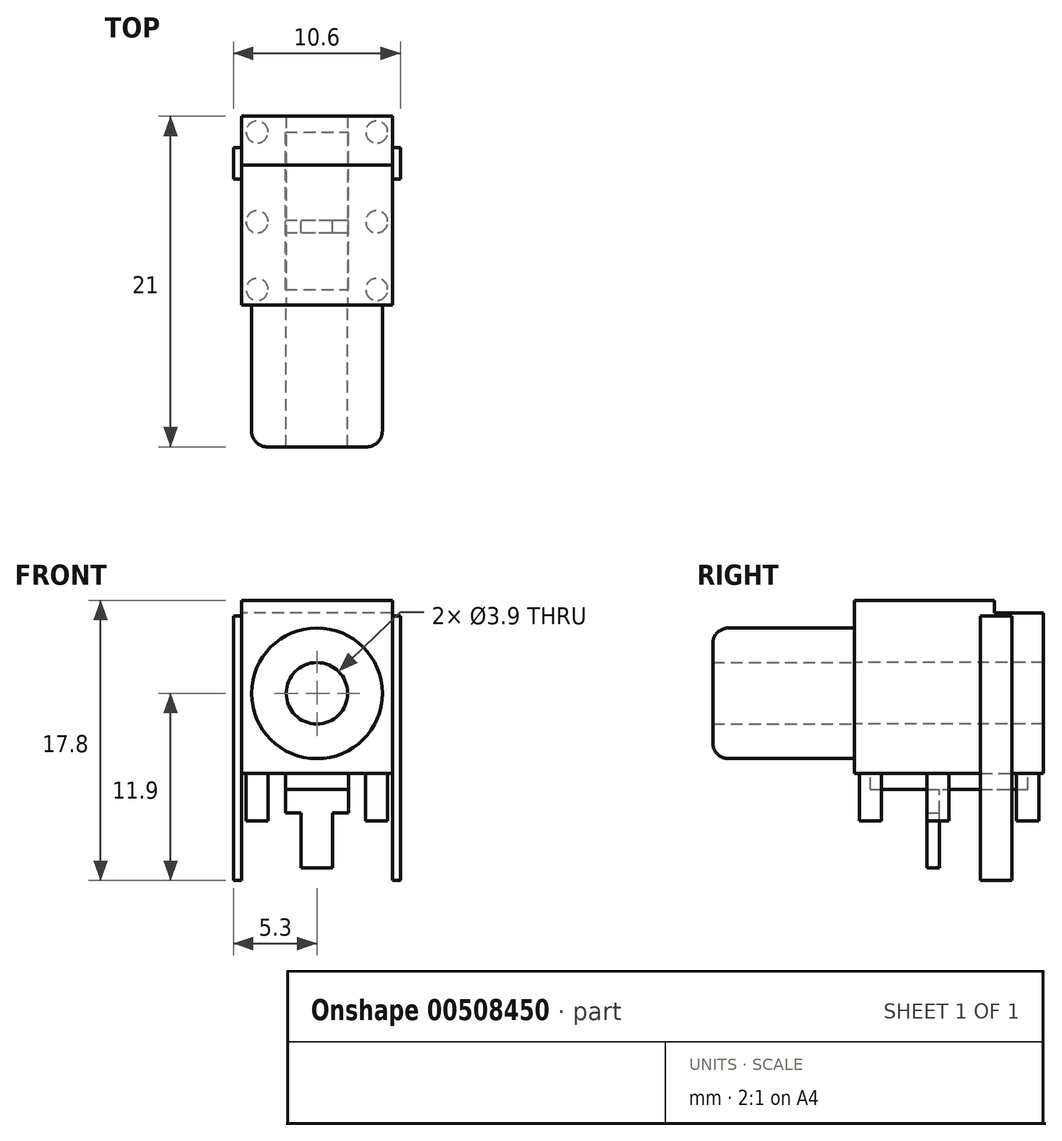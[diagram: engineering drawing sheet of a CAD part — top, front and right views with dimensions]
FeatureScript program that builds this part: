
annotation { "Feature Type Name" : "Feature", "Feature Type Description" : "" }
export const myFeature = defineFeature(function(context is Context, id is Id, definition is map)
    precondition{}
    {
        {
            var Q0;
            Q0=qCreatedBy(makeId("Front.planeOp"),FACE);
            var sketch = newSketch(context, id + "F0", { "sketchPlane" : qUnion([Q0])});
            skLineSegment(sketch, "E0.bottom", {"start": v(-4.8, 5.9) * mm, "end": v(4.8, 5.9) * mm});
            skLineSegment(sketch, "E0.top", {"start": v(-4.8, -5.1) * mm, "end": v(4.8, -5.1) * mm});
            skLineSegment(sketch, "E0.left", {"start": v(-4.8, 5.9) * mm, "end": v(-4.8, -5.1) * mm});
            skLineSegment(sketch, "E0.right", {"start": v(4.8, 5.9) * mm, "end": v(4.8, -5.1) * mm});
            skPoint(sketch, "E1", {"position": v(0, -5.1) * mm});
            skLineSegment(sketch, "E2", {"start": v(0, -5.1) * mm, "end": v(0, 0) * mm, "construction": true});
            skSolve(sketch);
        }
        {
            var Q0;
            Q0=makeQuery(id+"F0.imprint","IMPRINT",FACE,{"disambiguationData":[TD([[makeQuery(id+"F0.imprint","IMPRINT",EDGE,{"derivedFrom":sQuery(id+"F0.wireOp",EDGE,"E0.bottom")}),-1.0]])]});
            extrude(context, id + "F1", {"entities" : qUnion([Q0]), "depth" : 8.9 * mm});
        }
        {
            var Q0;
            Q0=makeQuery(id+"F1.opExtrude","CAP_FACE",FACE,{"disambiguationData":[OSD([sQuery(id+"F0.wireOp",EDGE,"E0.bottom"),sQuery(id+"F0.wireOp",EDGE,"E0.top"),sQuery(id+"F0.wireOp",EDGE,"E0.left"),sQuery(id+"F0.wireOp",EDGE,"E0.right")])],"isStart":true});
            var sketch = newSketch(context, id + "F2", { "sketchPlane" : qUnion([Q0])});
            skLineSegment(sketch, "E3.bottom", {"start": v(-4.8, -5.1) * mm, "end": v(4.8, -5.1) * mm});
            skLineSegment(sketch, "E3.top", {"start": v(-4.8, 5.1) * mm, "end": v(4.8, 5.1) * mm});
            skLineSegment(sketch, "E3.left", {"start": v(-4.8, -5.1) * mm, "end": v(-4.8, 5.1) * mm});
            skLineSegment(sketch, "E3.right", {"start": v(4.8, -5.1) * mm, "end": v(4.8, 5.1) * mm});
            skSolve(sketch);
        }
        {
            var Q0;
            Q0=makeQuery(id+"F2.imprint","IMPRINT",FACE,{"disambiguationData":[TD([[makeQuery(id+"F2.imprint","IMPRINT",EDGE,{"derivedFrom":sQuery(id+"F2.wireOp",EDGE,"E3.bottom")}),-1.0]])]});
            extrude(context, id + "F3", {"entities" : qUnion([Q0]), "operationType" : NewBodyOperationType.ADD, "depth" : 3.1 * mm});
        }
        {
            var Q0;
            Q0=makeQuery(id+"F3.boolean.opBoolean","MERGE",FACE,{"derivedFrom":[makeQuery(id+"F1.opExtrude","SWEPT_FACE",FACE,{"disambiguationData":[OSD([sQuery(id+"F0.wireOp",EDGE,"E0.top")])]}),makeQuery(id+"F3.opExtrude","SWEPT_FACE",FACE,{"disambiguationData":[OSD([sQuery(id+"F2.wireOp",EDGE,"E3.bottom")])]})]});
            var sketch = newSketch(context, id + "F4", { "sketchPlane" : qUnion([Q0])});
            skLineSegment(sketch, "E4", {"start": v(-3.8, 8.9) * mm, "end": v(-3.8, -3.1) * mm, "construction": true});
            skLineSegment(sketch, "E5", {"start": v(-3.8, 8.9) * mm, "end": v(-4.8, 8.9) * mm, "construction": true});
            skLineSegment(sketch, "E6", {"start": v(3.8, 8.9) * mm, "end": v(3.8, -3.1) * mm, "construction": true});
            skLineSegment(sketch, "E7", {"start": v(3.8, 8.9) * mm, "end": v(4.8, 8.9) * mm, "construction": true});
            skLineSegment(sketch, "E8", {"start": v(-4.8, 7.9) * mm, "end": v(4.8, 7.9) * mm, "construction": true});
            skLineSegment(sketch, "E9", {"start": v(4.8, 3.6) * mm, "end": v(-4.8, 3.6) * mm, "construction": true});
            skLineSegment(sketch, "E10", {"start": v(-4.8, -2.1) * mm, "end": v(4.8, -2.1) * mm, "construction": true});
            skCircle(sketch, "E11", {"center": v(-3.8, 7.9) * mm, "radius": 0.7 * mm});
            skCircle(sketch, "E12", {"center": v(-3.8, 3.6) * mm, "radius": 0.7 * mm});
            skCircle(sketch, "E13", {"center": v(-3.8, -2.1) * mm, "radius": 0.7 * mm});
            skCircle(sketch, "E14", {"center": v(3.8, -2.1) * mm, "radius": 0.7 * mm});
            skCircle(sketch, "E15", {"center": v(3.8, 3.6) * mm, "radius": 0.7 * mm});
            skCircle(sketch, "E16", {"center": v(3.8, 7.9) * mm, "radius": 0.7 * mm});
            skLineSegment(sketch, "E17.bottom", {"start": v(-2, 7.9) * mm, "end": v(2, 7.9) * mm});
            skLineSegment(sketch, "E17.top", {"start": v(-2, -2.1) * mm, "end": v(2, -2.1) * mm});
            skLineSegment(sketch, "E17.left", {"start": v(-2, 7.9) * mm, "end": v(-2, -2.1) * mm});
            skLineSegment(sketch, "E17.right", {"start": v(2, 7.9) * mm, "end": v(2, -2.1) * mm});
            skLineSegment(sketch, "E18", {"start": v(-4.8, 8.9) * mm, "end": v(-4.8, 7.9) * mm, "construction": true});
            skLineSegment(sketch, "E19", {"start": v(-4.8, 7.9) * mm, "end": v(-4.8, 3.6) * mm, "construction": true});
            skLineSegment(sketch, "E20", {"start": v(-4.8, -2.1) * mm, "end": v(-4.8, -3.1) * mm, "construction": true});
            skPoint(sketch, "E21", {"position": v(0, -2.1) * mm});
            skLineSegment(sketch, "E22", {"start": v(0, -2.1) * mm, "end": v(0, 0) * mm, "construction": true});
            skLineSegment(sketch, "E23.bottom", {"start": v(-4.8, 0.9) * mm, "end": v(-5.3, 0.9) * mm});
            skLineSegment(sketch, "E23.top", {"start": v(-4.8, -1.1) * mm, "end": v(-5.3, -1.1) * mm});
            skLineSegment(sketch, "E23.left", {"start": v(-4.8, 0.9) * mm, "end": v(-4.8, -1.1) * mm});
            skLineSegment(sketch, "E23.right", {"start": v(-5.3, 0.9) * mm, "end": v(-5.3, -1.1) * mm});
            skLineSegment(sketch, "E24.bottom", {"start": v(4.8, 0.9) * mm, "end": v(5.3, 0.9) * mm});
            skLineSegment(sketch, "E24.top", {"start": v(4.8, -1.1) * mm, "end": v(5.3, -1.1) * mm});
            skLineSegment(sketch, "E24.left", {"start": v(4.8, 0.9) * mm, "end": v(4.8, -1.1) * mm});
            skLineSegment(sketch, "E24.right", {"start": v(5.3, 0.9) * mm, "end": v(5.3, -1.1) * mm});
            skLineSegment(sketch, "E25", {"start": v(-4.8, 3.6) * mm, "end": v(-4.8, 0.9) * mm, "construction": true});
            skLineSegment(sketch, "E26", {"start": v(4.8, 3.6) * mm, "end": v(4.8, 0.9) * mm, "construction": true});
            skSolve(sketch);
        }
        {
            var Q0;
            Q0=makeQuery(id+"F4.imprint","IMPRINT",FACE,{"disambiguationData":[TD([[makeQuery(id+"F4.imprint","IMPRINT",EDGE,{"derivedFrom":sQuery(id+"F4.wireOp",EDGE,"E11")}),1.0]])]});
            var Q1;
            Q1=makeQuery(id+"F4.imprint","IMPRINT",FACE,{"disambiguationData":[TD([[makeQuery(id+"F4.imprint","IMPRINT",EDGE,{"derivedFrom":sQuery(id+"F4.wireOp",EDGE,"E12")}),1.0]])]});
            var Q2;
            Q2=makeQuery(id+"F4.imprint","IMPRINT",FACE,{"disambiguationData":[TD([[makeQuery(id+"F4.imprint","IMPRINT",EDGE,{"derivedFrom":sQuery(id+"F4.wireOp",EDGE,"E13")}),1.0]])]});
            var Q3;
            Q3=makeQuery(id+"F4.imprint","IMPRINT",FACE,{"disambiguationData":[TD([[makeQuery(id+"F4.imprint","IMPRINT",EDGE,{"derivedFrom":sQuery(id+"F4.wireOp",EDGE,"E14")}),1.0]])]});
            var Q4;
            Q4=makeQuery(id+"F4.imprint","IMPRINT",FACE,{"disambiguationData":[TD([[makeQuery(id+"F4.imprint","IMPRINT",EDGE,{"derivedFrom":sQuery(id+"F4.wireOp",EDGE,"E15")}),1.0]])]});
            var Q5;
            Q5=makeQuery(id+"F4.imprint","IMPRINT",FACE,{"disambiguationData":[TD([[makeQuery(id+"F4.imprint","IMPRINT",EDGE,{"derivedFrom":sQuery(id+"F4.wireOp",EDGE,"E16")}),1.0]])]});
            extrude(context, id + "F5", {"entities" : qUnion([Q0, Q1, Q2, Q3, Q4, Q5]), "operationType" : NewBodyOperationType.ADD, "depth" : 3 * mm});
        }
        {
            var Q0;
            Q0=makeQuery(id+"F4.imprint","IMPRINT",FACE,{"disambiguationData":[TD([[makeQuery(id+"F4.imprint","IMPRINT",EDGE,{"derivedFrom":sQuery(id+"F4.wireOp",EDGE,"E17.bottom")}),-1.0]])]});
            extrude(context, id + "F6", {"entities" : qUnion([Q0]), "operationType" : NewBodyOperationType.ADD, "depth" : 1 * mm});
        }
        {
            var Q0;
            Q0=makeQuery(id+"F4.imprint","IMPRINT",FACE,{"disambiguationData":[TD([[makeQuery(id+"F4.imprint","IMPRINT",EDGE,{"derivedFrom":sQuery(id+"F4.wireOp",EDGE,"E24.bottom")}),-1.0]])]});
            var Q1;
            Q1=makeQuery(id+"F4.imprint","IMPRINT",FACE,{"disambiguationData":[TD([[makeQuery(id+"F4.imprint","IMPRINT",EDGE,{"derivedFrom":sQuery(id+"F4.wireOp",EDGE,"E23.bottom")}),1.0]])]});
            extrude(context, id + "F7", {"entities" : qUnion([Q0, Q1]), "depth" : -10 * mm});
        }
        {
            var Q0;
            Q0=makeQuery(id+"F4.imprint","IMPRINT",FACE,{"disambiguationData":[TD([[makeQuery(id+"F4.imprint","IMPRINT",EDGE,{"derivedFrom":sQuery(id+"F4.wireOp",EDGE,"E23.bottom")}),1.0]])]});
            extrude(context, id + "F8", {"entities" : qUnion([Q0]), "operationType" : NewBodyOperationType.ADD, "depth" : 6.8 * mm});
        }
        {
            var Q0;
            Q0=makeQuery(id+"F6.opExtrude","CAP_FACE",FACE,{"disambiguationData":[OSD([sQuery(id+"F4.wireOp",EDGE,"E17.bottom"),sQuery(id+"F4.wireOp",EDGE,"E17.top"),sQuery(id+"F4.wireOp",EDGE,"E17.left"),sQuery(id+"F4.wireOp",EDGE,"E17.right")])],"isStart":false});
            var sketch = newSketch(context, id + "F9", { "sketchPlane" : qUnion([Q0])});
            skLineSegment(sketch, "E27.bottom", {"start": v(-2, 4.3) * mm, "end": v(2, 4.3) * mm});
            skLineSegment(sketch, "E27.top", {"start": v(-2, 3.5) * mm, "end": v(2, 3.5) * mm});
            skLineSegment(sketch, "E27.left", {"start": v(-2, 4.3) * mm, "end": v(-2, 3.5) * mm});
            skLineSegment(sketch, "E27.right", {"start": v(2, 4.3) * mm, "end": v(2, 3.5) * mm});
            skPoint(sketch, "E28", {"position": v(0, 3.5) * mm});
            skLineSegment(sketch, "E29", {"start": v(0, 3.5) * mm, "end": v(0, 4.15) * mm, "construction": true});
            skPoint(sketch, "E30", {"position": v(-2, 3.9) * mm});
            skLineSegment(sketch, "E31", {"start": v(-2, 3.9) * mm, "end": v(-2, 7.9) * mm, "construction": true});
            skSolve(sketch);
        }
        {
            var Q0;
            Q0=makeQuery(id+"F9.imprint","IMPRINT",FACE,{"disambiguationData":[TD([[makeQuery(id+"F9.imprint","IMPRINT",EDGE,{"derivedFrom":sQuery(id+"F9.wireOp",EDGE,"E27.bottom")}),-1.0]])]});
            extrude(context, id + "F10", {"entities" : qUnion([Q0]), "depth" : 1.5 * mm});
        }
        {
            var Q0;
            Q0=makeQuery(id+"F4.imprint","IMPRINT",FACE,{"disambiguationData":[TD([[makeQuery(id+"F4.imprint","IMPRINT",EDGE,{"derivedFrom":sQuery(id+"F4.wireOp",EDGE,"E24.bottom")}),-1.0]])]});
            extrude(context, id + "F11", {"entities" : qUnion([Q0]), "operationType" : NewBodyOperationType.ADD, "depth" : 6.8 * mm});
        }
        {
            var Q0;
            Q0=makeQuery(id+"F1.opExtrude","CAP_FACE",FACE,{"disambiguationData":[OSD([sQuery(id+"F0.wireOp",EDGE,"E0.bottom"),sQuery(id+"F0.wireOp",EDGE,"E0.top"),sQuery(id+"F0.wireOp",EDGE,"E0.left"),sQuery(id+"F0.wireOp",EDGE,"E0.right")])],"isStart":false});
            var sketch = newSketch(context, id + "F12", { "sketchPlane" : qUnion([Q0])});
            skCircle(sketch, "E32", {"center": v(0, 0) * mm, "radius": 1.95 * mm});
            skCircle(sketch, "E33", {"center": v(0, 0) * mm, "radius": 4.15 * mm});
            skSolve(sketch);
        }
        {
            var Q0;
            Q0=makeQuery(id+"F12.imprint","IMPRINT",FACE,{"disambiguationData":[TD([[makeQuery(id+"F12.imprint","IMPRINT",EDGE,{"derivedFrom":sQuery(id+"F12.wireOp",EDGE,"E32")}),-1.0]])]});
            extrude(context, id + "F13", {"entities" : qUnion([Q0]), "depth" : 9 * mm});
        }
        {
            var Q0;
            Q0=makeQuery(id+"F13.opExtrude","CAP_EDGE",EDGE,{"disambiguationData":[OSD([sQuery(id+"F12.wireOp",EDGE,"E33")])],"isStart":false});
            fillet(context, id + "F14", {"entities" : qUnion([Q0]), "radius" : 1 * mm, "tangentPropagation" : true, "allowEdgeOverflow" : false});
        }
        {
            var Q0;
            Q0=makeQuery(id+"F12.imprint","IMPRINT",FACE,{"disambiguationData":[TD([[makeQuery(id+"F12.imprint","IMPRINT",EDGE,{"derivedFrom":sQuery(id+"F12.wireOp",EDGE,"E32")}),1.0]])]});
            extrude(context, id + "F15", {"entities" : qUnion([Q0]), "operationType" : NewBodyOperationType.REMOVE, "oppositeDirection" : true, "depth" : 12 * mm});
        }
        {
            var Q0;
            Q0=makeQuery(id+"F10.opExtrude","CAP_FACE",FACE,{"disambiguationData":[OSD([sQuery(id+"F9.wireOp",EDGE,"E27.bottom"),sQuery(id+"F9.wireOp",EDGE,"E27.top"),sQuery(id+"F9.wireOp",EDGE,"E27.left"),sQuery(id+"F9.wireOp",EDGE,"E27.right")])],"isStart":false});
            var sketch = newSketch(context, id + "F16", { "sketchPlane" : qUnion([Q0])});
            skLineSegment(sketch, "E34.bottom", {"start": v(-1, 4.3) * mm, "end": v(1, 4.3) * mm});
            skLineSegment(sketch, "E34.top", {"start": v(-1, 3.5) * mm, "end": v(1, 3.5) * mm});
            skLineSegment(sketch, "E34.left", {"start": v(-1, 4.3) * mm, "end": v(-1, 3.5) * mm});
            skLineSegment(sketch, "E34.right", {"start": v(1, 4.3) * mm, "end": v(1, 3.5) * mm});
            skPoint(sketch, "E35", {"position": v(0, 4.3) * mm});
            skSolve(sketch);
        }
        {
            var Q0;
            Q0=makeQuery(id+"F16.imprint","IMPRINT",FACE,{"disambiguationData":[TD([[makeQuery(id+"F16.imprint","IMPRINT",EDGE,{"derivedFrom":sQuery(id+"F16.wireOp",EDGE,"E34.bottom")}),-1.0]])]});
            extrude(context, id + "F17", {"entities" : qUnion([Q0]), "operationType" : NewBodyOperationType.ADD, "depth" : 3.5 * mm});
        }
    });
